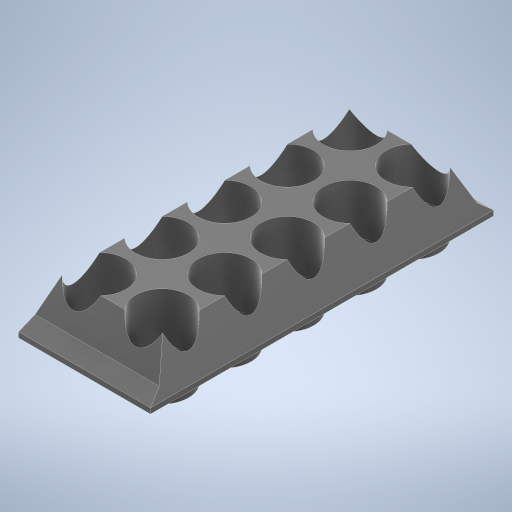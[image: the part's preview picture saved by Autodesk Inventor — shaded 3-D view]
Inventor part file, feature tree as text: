
AUTODESK INVENTOR PART (.ipt)
format: ipt  version: 2023 (Build 270158000, 158)  size: 440,832 bytes
history: native  units: mm
features: extrude x4, sketch x3, shell x1
ambient origin geometry x8: Origin, YZ Plane, XZ Plane, XY Plane, X Axis, Y Axis, Z Axis, Center Point
bodies: Solid1 (feature_tree)
feature tree (8):
  extrude  "Extrusion1"  Depth=95.0mm
  extrude  "Extrusion2"  Depth=20.071286mm
  sketch  "Sketch4"  dims[d8=260.0mm d9=20.071286mm d10=75.0mm d11=200.0mm d12=0.0mm d13=3.490659mm d14=3.490659mm d15=200.0mm d16=0.0mm d17=80.0mm d18=80.0mm d19=80.0mm d20=80.0mm d21=80.0mm d22=80.0mm d23=80.0mm d24=80.0mm d25=80.0mm d26=80.0mm d27=95.0mm d29=52.5mm d32=95.0mm d33=70.0mm d34=95.0mm d35=95.0mm d36=95.0mm d37=0.0mm d38=0.0mm d39=20.0mm d40=0.0mm d41=1.0mm]
  extrude  "Extrusion3"  Depth=1.0mm
  extrude  "Extrusion4"  Depth=75.0mm
  shell  "Shell1"  Thickness=200.0mm
  sketch  "Sketch1"  dims[d2=520.0mm d3=95.0mm d4=8.0mm]
  sketch  "Sketch3"  dims[d5=22.68928mm d6=20.071286mm d7=25.0mm]
